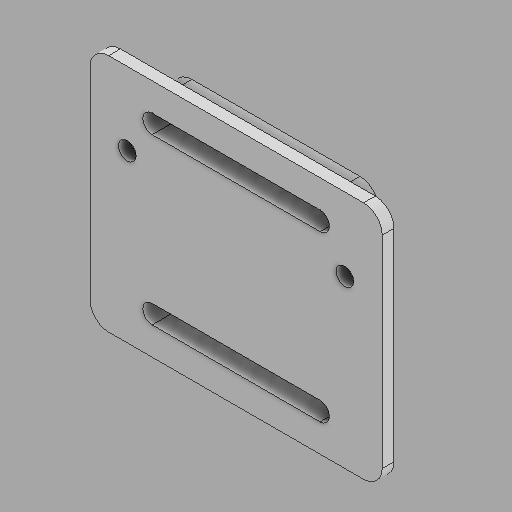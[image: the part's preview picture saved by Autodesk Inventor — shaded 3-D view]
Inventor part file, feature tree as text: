
AUTODESK INVENTOR PART (.ipt)
format: ipt  version: 2025.2 (Build 292293000, 293)  size: 160,256 bytes
history: native  units: in
note: dims shown in document units (in); Inventor stores cm internally (conversion verified against a paired STEP export)
features: sketch x4, extrude x3, projected_geometry x2, hole x1, fillet x1
ambient origin geometry x8: Origin, YZ Plane, XZ Plane, XY Plane, X Axis, Y Axis, Z Axis, Center Point
bodies: Solid1 (feature_tree)
feature tree (11):
  extrude  "Extrusion1"  Depth=1.6031in
  sketch  "Sketch3"  dims[d2=0.0787in d3=0.0in d17=1.4567in]
  hole  "Hole1"  [1 undecoded]
  fillet  "Fillet1"  Radius=0.3125in
  extrude  "Extrusion4"  Depth=0.125in
  extrude  "Extrusion5"  Depth=1.1031in
  sketch  "Sketch1"  dims[d0=1.9567in d1=1.6031in]
  sketch  "Sketch5"  dims[d19=0.1181in d20=0.75in d21=0.375in d22=0.25in d23=0.5635in d24=1.0in d25=0.8108in d26=0.3125in]
  sketch  "Sketch6"  dims[d27=0.125in d28=0.125in d29=1.1031in d30=1.125in d31=0.1875in d32=0.0in d33=0.0625in d34=0.0in d35=0.0in]
  projected_geometry  "Projected Loop2"
  projected_geometry  "Projected Loop3"
note: 1 required parameter value undecoded (feature->parameter linkage not recoverable at this tier; creation-order binding heuristic only, values carry confidence <= 0.55)
